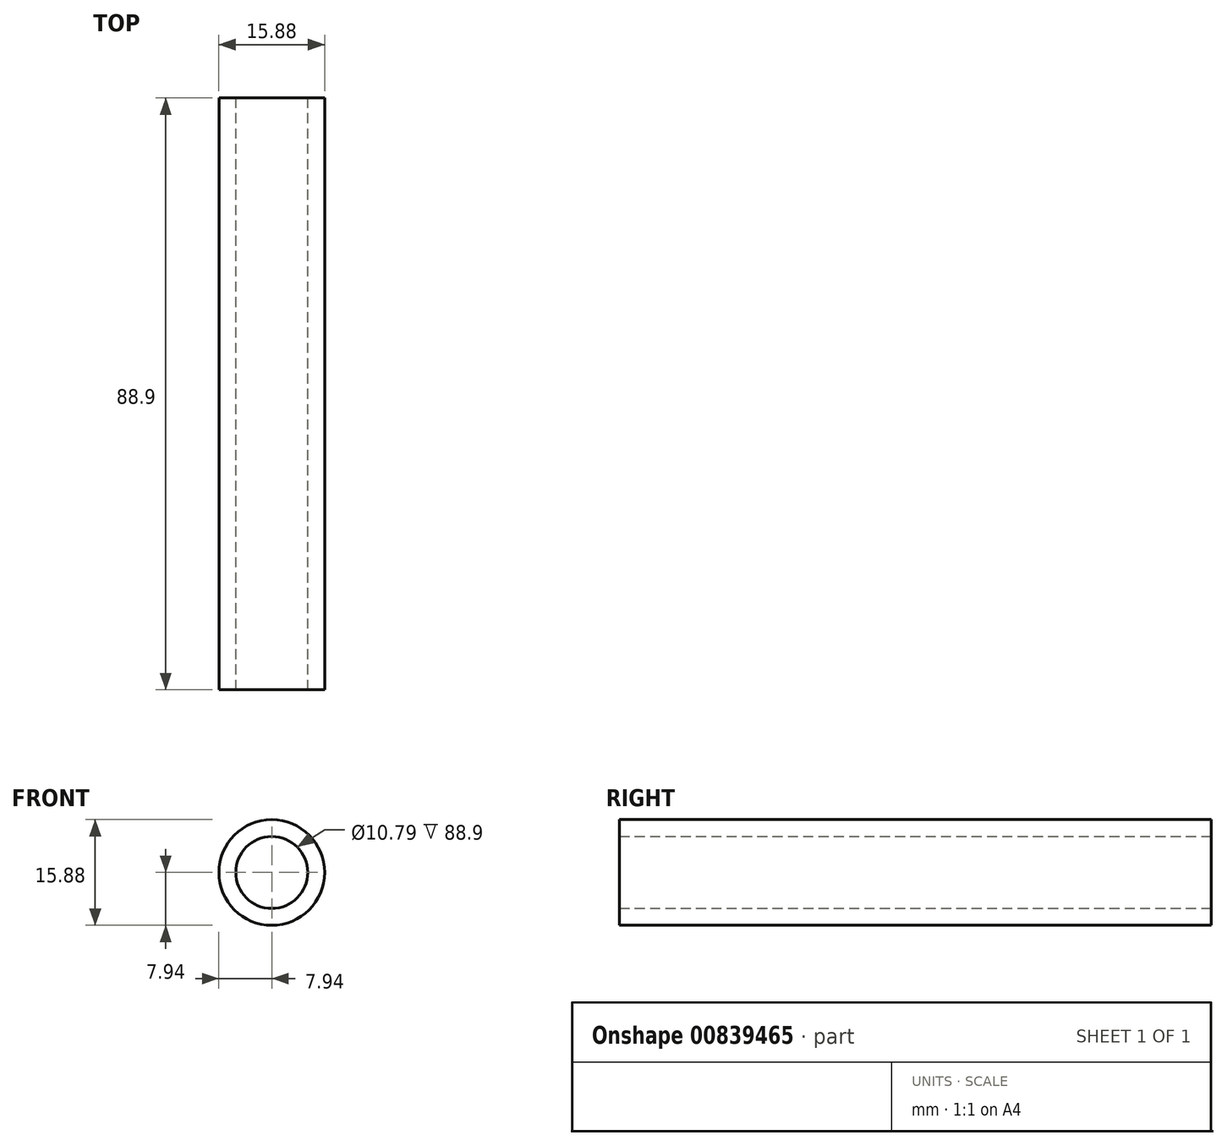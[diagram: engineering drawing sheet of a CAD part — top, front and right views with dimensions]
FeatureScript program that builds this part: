
annotation { "Feature Type Name" : "Feature", "Feature Type Description" : "" }
export const myFeature = defineFeature(function(context is Context, id is Id, definition is map)
    precondition{}
    {
        {
            var Q0;
            Q0=qCreatedBy(makeId("Front.planeOp"),FACE);
            var sketch = newSketch(context, id + "F0", { "sketchPlane" : qUnion([Q0])});
            skCircle(sketch, "E0", {"center": v(0, 0) * mm, "radius": 7.94 * mm});
            skCircle(sketch, "E1", {"center": v(0, 0) * mm, "radius": 5.4 * mm});
            skSolve(sketch);
        }
        {
            var Q0;
            Q0=makeQuery(id+"F0.imprint","IMPRINT",FACE,{"disambiguationData":[TD([[makeQuery(id+"F0.imprint","IMPRINT",EDGE,{"derivedFrom":sQuery(id+"F0.wireOp",EDGE,"E0")}),1.0]])]});
            extrude(context, id + "F1", {"entities" : qUnion([Q0]), "depth" : 88.9 * mm, "offsetDistance" : 25.4 * mm});
        }
    });
